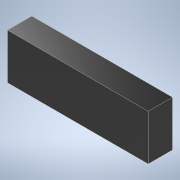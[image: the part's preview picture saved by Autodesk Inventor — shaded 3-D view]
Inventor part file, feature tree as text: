
AUTODESK INVENTOR PART (.ipt)
format: ipt  version: 2021 (Build 250183000, 183)  size: 88,576 bytes
history: native  units: mm
features: extrude x1, sketch x1
ambient origin geometry x8: Origin, YZ Plane, XZ Plane, XY Plane, X Axis, Y Axis, Z Axis, Center Point
bodies: Solid1 (feature_tree)
feature tree (2):
  extrude  "Extrusion1"  Depth=47.0mm
  sketch  "Sketch1"  dims[d0=145.0mm d1=47.0mm d2=25.0mm d3=0.0mm]
